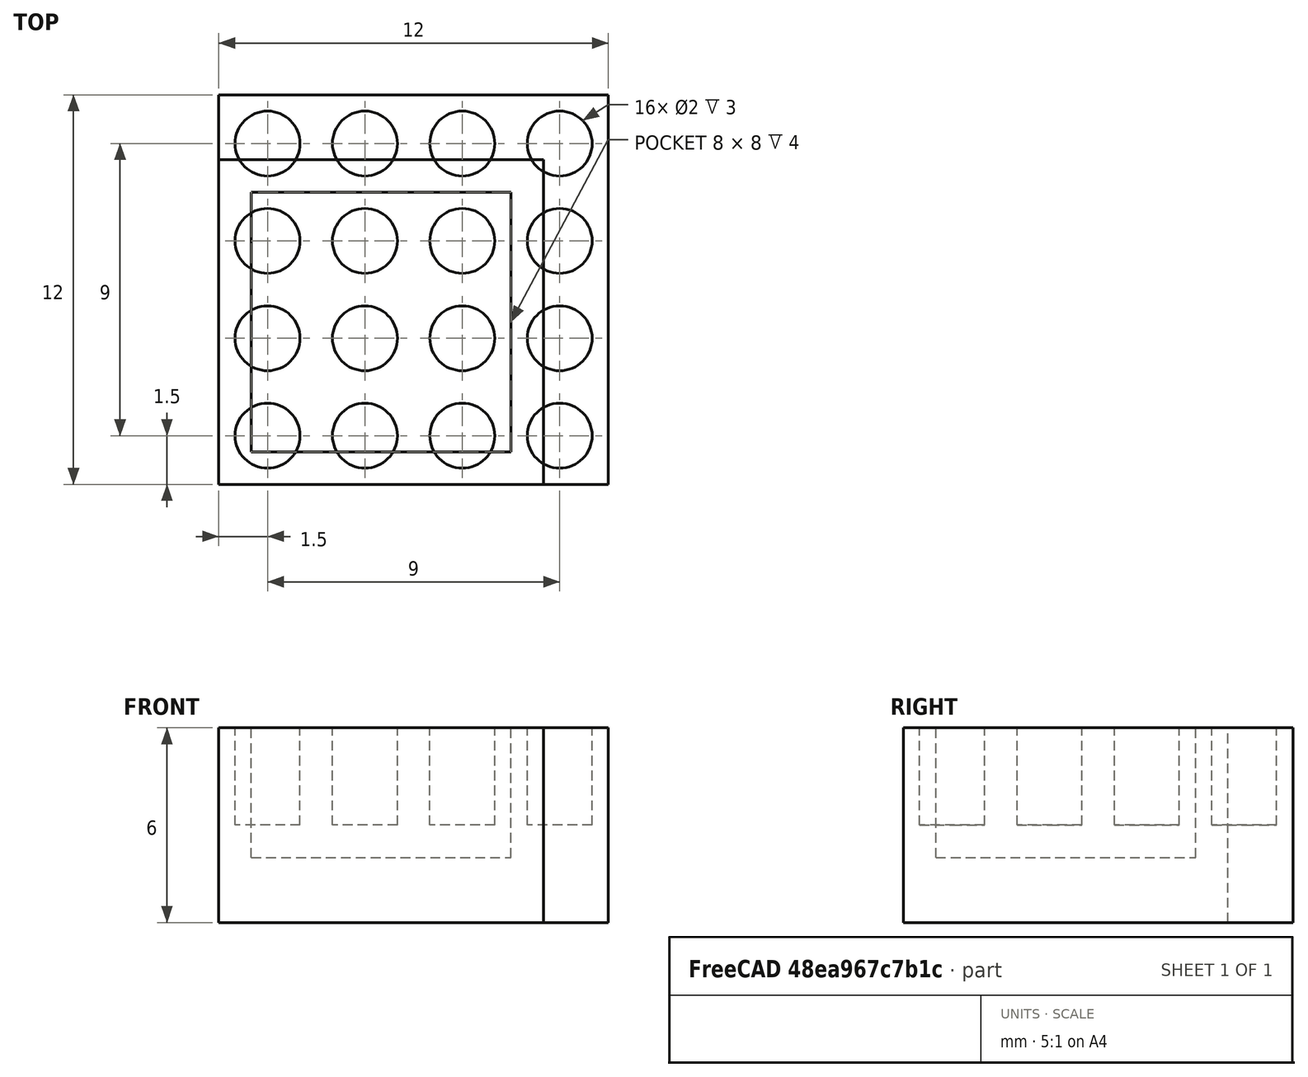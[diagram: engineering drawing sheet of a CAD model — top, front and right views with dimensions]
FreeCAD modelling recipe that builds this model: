
FCSTD DOCUMENT  (FreeCAD 0.18R16033 (Git))
Label: pegs
License: All rights reserved
LicenseURL: http://en.wikipedia.org/wiki/All_rights_reserved
objects: Part::Box×3, Part::Cut×2, Part::Cylinder×1, Part::FeaturePython×1
note: 7 computed .brp shape members not serialized (recipe doc carries the construction recipe); baked Part::Feature solids carry a one-line shape summary decoded from their .brp

FEATURE [Part::Box] Box  label="Cube"
  AttacherType = Attacher::AttachEngine3D
  Height = 6
  Length = 12
  Width = 12
FEATURE [Part::Cylinder] Cylinder
  Angle = 360
  AttacherType = Attacher::AttachEngine3D
  Height = 3
  Placement = pos=(0,0,3) rot=(0,0,1;0rad)
  Radius = 1
  expr: Radius = 2 / 2
FEATURE [Part::FeaturePython] Array  # Draft array (typed FeaturePython)
  Angle = 360
  ArrayType = 0
  Axis = (0,0,1)
  Base = -> Cylinder
  Center = (0,0,0)
  Fuse = false
  IntervalAxis = (0,0,0)
  IntervalX = (3,0,0)
  IntervalY = (0,3,0)
  IntervalZ = (0,0,1)
  NumberPolar = 1
  NumberX = 4
  NumberY = 4
  NumberZ = 1
  Placement = pos=(1.5,1.5,0) rot=(0,0,1;0rad)
FEATURE [Part::Cut] Cut
  Base = -> Box
  Tool = -> Array
FEATURE [Part::Box] Box001  label="Cube001"
  AttacherType = Attacher::AttachEngine3D
  Height = 6
  Length = 10
  Width = 10
FEATURE [Part::Box] Box002  label="Cube002"
  AttacherType = Attacher::AttachEngine3D
  Height = 6
  Length = 8
  Placement = pos=(1,1,2) rot=(0,0,1;0rad)
  Width = 8
FEATURE [Part::Cut] Cut001
  Base = -> Box001
  Tool = -> Box002
